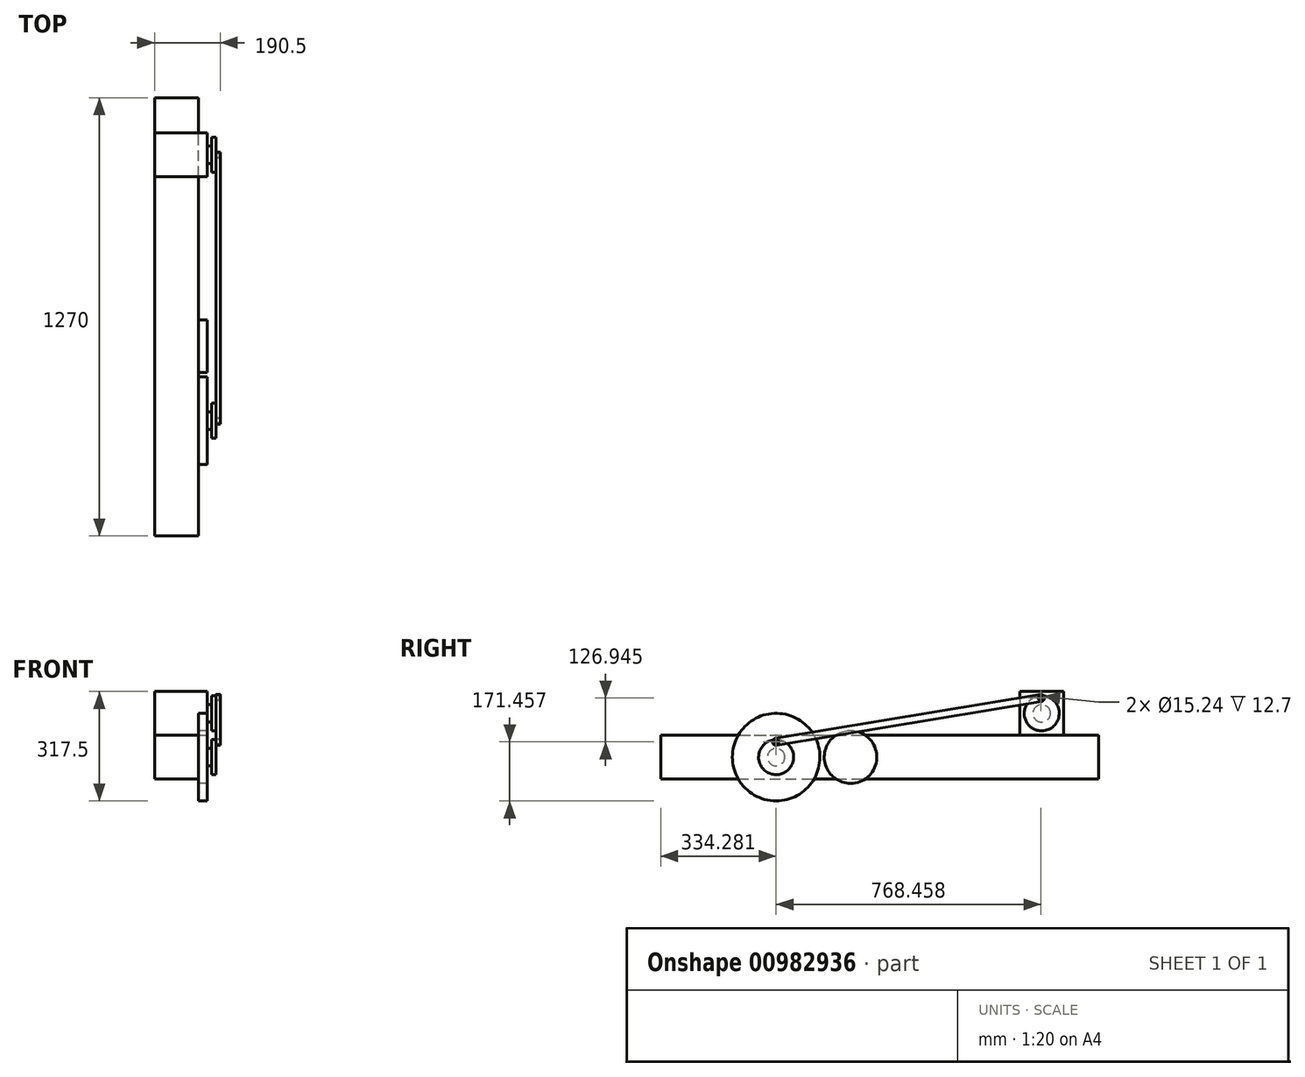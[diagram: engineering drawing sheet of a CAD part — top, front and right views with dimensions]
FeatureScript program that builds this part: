
annotation { "Feature Type Name" : "Feature", "Feature Type Description" : "" }
export const myFeature = defineFeature(function(context is Context, id is Id, definition is map)
    precondition{}
    {
        {
            var Q0;
            Q0=qCreatedBy(makeId("Right.planeOp"),FACE);
            var sketch = newSketch(context, id + "F0", { "sketchPlane" : qUnion([Q0])});
            skLineSegment(sketch, "E0.bottom", {"start": v(0, 0) * mm, "end": v(1270, 0) * mm});
            skLineSegment(sketch, "E0.top", {"start": v(0, -127) * mm, "end": v(1270, -127) * mm});
            skLineSegment(sketch, "E0.left", {"start": v(0, 0) * mm, "end": v(0, -127) * mm});
            skLineSegment(sketch, "E0.right", {"start": v(1270, 0) * mm, "end": v(1270, -127) * mm});
            skSolve(sketch);
        }
        {
            var Q0;
            Q0=qSketchRegion(id+"F0",true);
            extrude(context, id + "F1", {"entities" : qUnion([Q0]), "oppositeDirection" : true, "depth" : 127 * mm, "offsetDistance" : 25.4 * mm});
        }
        {
            var Q0;
            Q0=makeQuery(id+"F1.opExtrude","CAP_FACE",FACE,{"disambiguationData":[OSD([sQuery(id+"F0.wireOp",EDGE,"E0.bottom"),sQuery(id+"F0.wireOp",EDGE,"E0.top"),sQuery(id+"F0.wireOp",EDGE,"E0.left"),sQuery(id+"F0.wireOp",EDGE,"E0.right")])],"isStart":true});
            var sketch = newSketch(context, id + "F2", { "sketchPlane" : qUnion([Q0])});
            skCircle(sketch, "E1", {"center": v(334.44, -63.5) * mm, "radius": 127 * mm});
            skPoint(sketch, "E1.centerSnap0", {"position": v(0, -63.5) * mm});
            skCircle(sketch, "E2", {"center": v(550.34, -63.5) * mm, "radius": 76.2 * mm});
            skSolve(sketch);
        }
        {
            var Q0;
            Q0=qSketchRegion(id+"F2",true);
            extrude(context, id + "F3", {"entities" : qUnion([Q0]), "operationType" : NewBodyOperationType.ADD, "depth" : 25.4 * mm, "offsetDistance" : 25.4 * mm});
        }
        {
            var Q0;
            Q0=makeQuery(id+"F3.opExtrude","CAP_FACE",FACE,{"disambiguationData":[OSD([sQuery(id+"F2.wireOp",EDGE,"E1")])],"isStart":false});
            var sketch = newSketch(context, id + "F4", { "sketchPlane" : qUnion([Q0])});
            skCircle(sketch, "E3", {"center": v(334.44, -63.5) * mm, "radius": 25.4 * mm});
            skSolve(sketch);
        }
        {
            var Q0;
            Q0=qSketchRegion(id+"F4",true);
            extrude(context, id + "F5", {"entities" : qUnion([Q0]), "operationType" : NewBodyOperationType.ADD, "depth" : 25.4 * mm, "offsetDistance" : 25.4 * mm});
        }
        {
            var Q0;
            Q0=makeQuery(id+"F1.opExtrude","SWEPT_FACE",FACE,{"disambiguationData":[OSD([sQuery(id+"F0.wireOp",EDGE,"E0.bottom")])]});
            var sketch = newSketch(context, id + "F6", { "sketchPlane" : qUnion([Q0])});
            skLineSegment(sketch, "E4.bottom", {"start": v(-127, 1168.4) * mm, "end": v(25.4, 1168.4) * mm});
            skLineSegment(sketch, "E4.top", {"start": v(-127, 1041.4) * mm, "end": v(25.4, 1041.4) * mm});
            skLineSegment(sketch, "E4.left", {"start": v(-127, 1168.4) * mm, "end": v(-127, 1041.4) * mm});
            skLineSegment(sketch, "E4.right", {"start": v(25.4, 1168.4) * mm, "end": v(25.4, 1041.4) * mm});
            skSolve(sketch);
        }
        {
            var Q0;
            Q0=qSketchRegion(id+"F6",true);
            extrude(context, id + "F7", {"entities" : qUnion([Q0]), "operationType" : NewBodyOperationType.ADD, "depth" : 127 * mm, "offsetDistance" : 25.4 * mm});
        }
        {
            var Q0;
            Q0=makeQuery(id+"F7.opExtrude","SWEPT_FACE",FACE,{"disambiguationData":[OSD([sQuery(id+"F6.wireOp",EDGE,"E4.right")])]});
            var sketch = newSketch(context, id + "F8", { "sketchPlane" : qUnion([Q0])});
            skCircle(sketch, "E5", {"center": v(1104.9, 63.5) * mm, "radius": 25.4 * mm});
            skPoint(sketch, "E5.centerSnap0", {"position": v(1041.4, 63.5) * mm});
            skPoint(sketch, "E5.centerSnap1", {"position": v(1104.9, 0) * mm});
            skSolve(sketch);
        }
        {
            var Q0;
            Q0=makeQuery(id+"F8.imprint","IMPRINT",FACE,{"disambiguationData":[TD([[makeQuery(id+"F8.imprint","IMPRINT",EDGE,{"derivedFrom":sQuery(id+"F8.wireOp",EDGE,"E5")}),1.0]])]});
            extrude(context, id + "F9", {"entities" : qUnion([Q0]), "operationType" : NewBodyOperationType.ADD, "depth" : 25.4 * mm, "offsetDistance" : 25.4 * mm});
        }
        {
            var Q0;
            Q0=makeQuery(id+"F9.opExtrude","CAP_FACE",FACE,{"disambiguationData":[OSD([sQuery(id+"F8.wireOp",EDGE,"E5")])],"isStart":false});
            var sketch = newSketch(context, id + "F10", { "sketchPlane" : qUnion([Q0])});
            skCircle(sketch, "E6", {"center": v(1104.9, 63.5) * mm, "radius": 50.8 * mm});
            skSolve(sketch);
        }
        {
            var Q0;
            Q0 = qSketchRegion(id + "F10", true);
            extrude(context, id + "F11", {"entities" : qUnion([Q0]), "operationType" : NewBodyOperationType.ADD, "oppositeDirection" : true, "depth" : 12.7 * mm, "offsetDistance" : 25.4 * mm});
        }
        {
            var Q0;
            Q0=makeQuery(id+"F5.opExtrude","CAP_FACE",FACE,{"disambiguationData":[OSD([sQuery(id+"F4.wireOp",EDGE,"E3")])],"isStart":false});
            var sketch = newSketch(context, id + "F12", { "sketchPlane" : qUnion([Q0])});
            skCircle(sketch, "E7", {"center": v(334.44, -63.5) * mm, "radius": 50.8 * mm});
            skSolve(sketch);
        }
        {
            var Q0;
            Q0 = qSketchRegion(id + "F12", true);
            extrude(context, id + "F13", {"entities" : qUnion([Q0]), "operationType" : NewBodyOperationType.ADD, "oppositeDirection" : true, "depth" : 12.7 * mm, "offsetDistance" : 25.4 * mm});
        }
        {
            var Q0;
            Q0=makeQuery(id+"F11.boolean.opBoolean","MERGE",FACE,{"derivedFrom":[makeQuery(id+"F9.opExtrude","CAP_FACE",FACE,{"disambiguationData":[OSD([sQuery(id+"F8.wireOp",EDGE,"E5")])],"isStart":false}),makeQuery(id+"F11.opExtrude","CAP_FACE",FACE,{"disambiguationData":[OSD([sQuery(id+"F10.wireOp",EDGE,"E6")])],"isStart":true})]});
            var sketch = newSketch(context, id + "F14", { "sketchPlane" : qUnion([Q0])});
            skCircle(sketch, "E8", {"center": v(1102.74, 107.9) * mm, "radius": 6.35 * mm});
            skPoint(sketch, "E8.first.point", {"position": v(1102.69, 114.25) * mm});
            skPoint(sketch, "E8.second.point", {"position": v(1108.1, 111.31) * mm});
            skPoint(sketch, "E8.third.point", {"position": v(1097.43, 111.38) * mm});
            skSolve(sketch);
        }
        {
            var Q0;
            Q0 = qSketchRegion(id + "F14", true);
            extrude(context, id + "F15", {"entities" : qUnion([Q0]), "operationType" : NewBodyOperationType.ADD, "depth" : 10.16 * mm, "offsetDistance" : 25.4 * mm});
        }
        {
            var Q0;
            Q0=makeQuery(id+"F13.boolean.opBoolean","MERGE",FACE,{"derivedFrom":[makeQuery(id+"F5.opExtrude","CAP_FACE",FACE,{"disambiguationData":[OSD([sQuery(id+"F4.wireOp",EDGE,"E3")])],"isStart":false}),makeQuery(id+"F13.opExtrude","CAP_FACE",FACE,{"disambiguationData":[OSD([sQuery(id+"F12.wireOp",EDGE,"E7")])],"isStart":true})]});
            var sketch = newSketch(context, id + "F16", { "sketchPlane" : qUnion([Q0])});
            skCircle(sketch, "E9", {"center": v(334.28, -19.04) * mm, "radius": 6.35 * mm});
            skPoint(sketch, "E9.first.point", {"position": v(333.93, -12.7) * mm});
            skPoint(sketch, "E9.second.point", {"position": v(340.63, -18.98) * mm});
            skPoint(sketch, "E9.third.point", {"position": v(327.99, -19.9) * mm});
            skSolve(sketch);
        }
        {
            var Q0;
            Q0 = qSketchRegion(id + "F16", true);
            extrude(context, id + "F17", {"entities" : qUnion([Q0]), "operationType" : NewBodyOperationType.ADD, "depth" : 12.7 * mm, "offsetDistance" : 25.4 * mm});
        }
        {
            var Q0;
            Q0=makeQuery(id+"F11.boolean.opBoolean","MERGE",FACE,{"derivedFrom":[makeQuery(id+"F9.opExtrude","CAP_FACE",FACE,{"disambiguationData":[OSD([sQuery(id+"F8.wireOp",EDGE,"E5")])],"isStart":false}),makeQuery(id+"F11.opExtrude","CAP_FACE",FACE,{"disambiguationData":[OSD([sQuery(id+"F10.wireOp",EDGE,"E6")])],"isStart":true})]});
            var sketch = newSketch(context, id + "F18", { "sketchPlane" : qUnion([Q0])});
            skLineSegment(sketch, "E10", {"start": v(1101.08, 117.93) * mm, "end": v(331.92, -9.14) * mm});
            skPoint(sketch, "E11.endSnap0", {"position": v(1103.05, 101.56) * mm});
            skLineSegment(sketch, "E12", {"start": v(1104.4, 97.88) * mm, "end": v(335.94, -29.07) * mm});
            skCircle(sketch, "E13", {"center": v(1102.74, 107.9) * mm, "radius": 7.62 * mm});
            skArc(sketch, "E14", {"start": v(1104.4, 97.88) * mm, "mid": v(1112.76, 109.56) * mm, "end": v(1101.08, 117.93) * mm});
            skArc(sketch, "E15", {"start": v(332.63, -9.02) * mm, "mid": v(324.26, -20.7) * mm, "end": v(335.94, -29.07) * mm});
            skPoint(sketch, "E15.third.point", {"position": v(344.61, -20.17) * mm});
            skCircle(sketch, "E16", {"center": v(334.28, -19.04) * mm, "radius": 7.62 * mm});
            skSolve(sketch);
        }
        {
            var Q0;
            Q0 = qSketchRegion(id + "F18", true);
            extrude(context, id + "F19", {"entities" : qUnion([Q0]), "operationType" : NewBodyOperationType.ADD, "depth" : 12.7 * mm, "offsetDistance" : 25.4 * mm});
        }
    });
